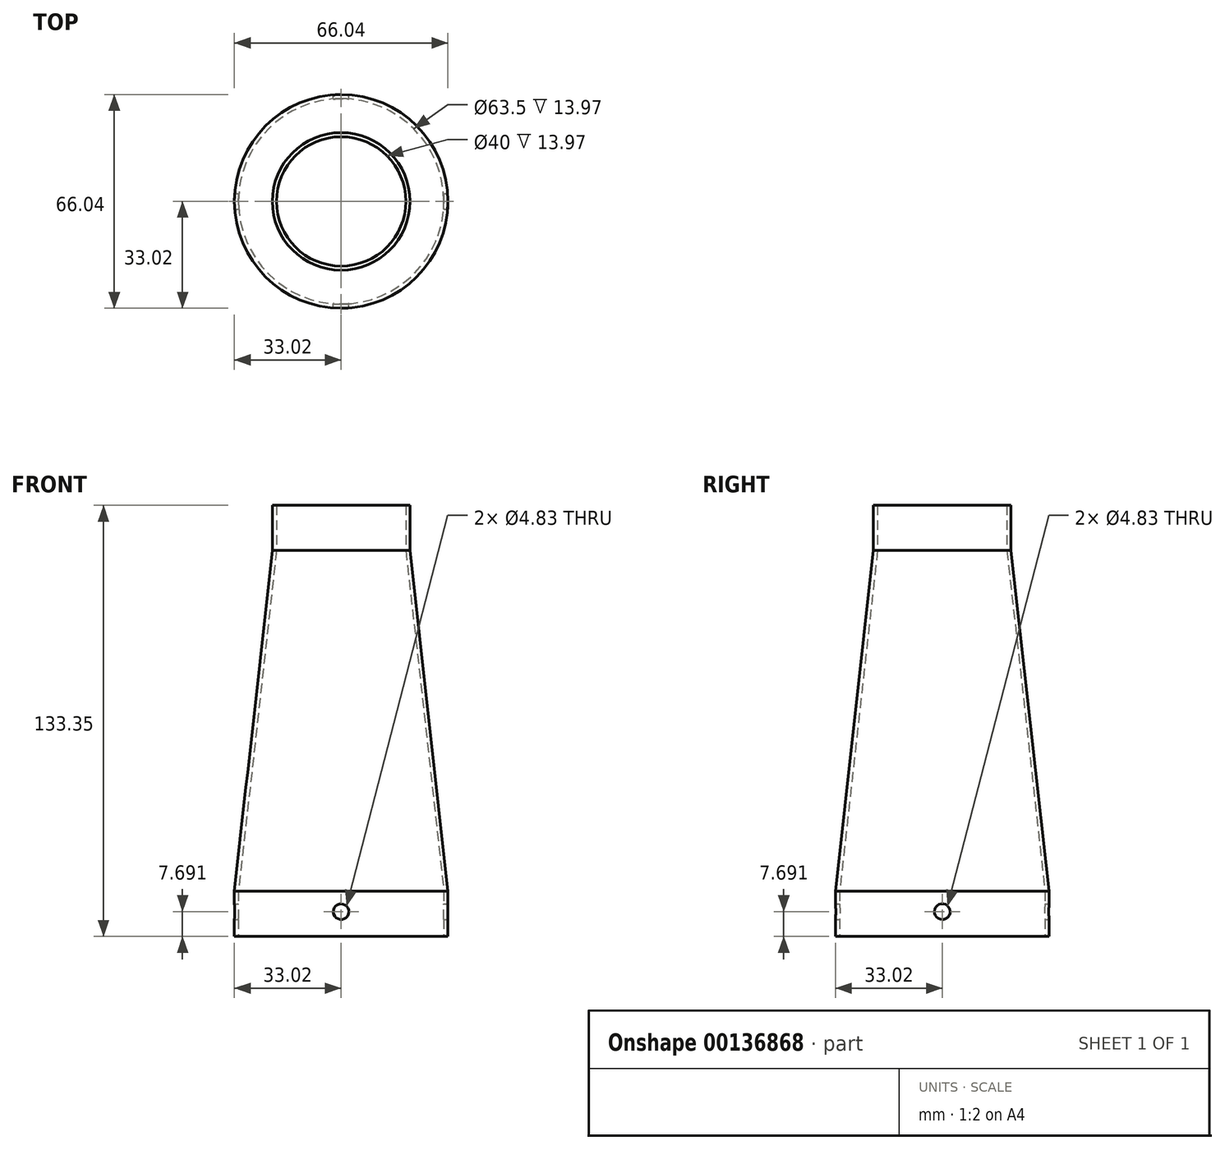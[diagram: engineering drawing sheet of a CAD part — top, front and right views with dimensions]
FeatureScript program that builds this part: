
annotation { "Feature Type Name" : "Feature", "Feature Type Description" : "" }
export const myFeature = defineFeature(function(context is Context, id is Id, definition is map)
    precondition{}
    {
        {
            var Q0;
            Q0=qCreatedBy(makeId("Front.planeOp"),FACE);
            var sketch = newSketch(context, id + "F0", { "sketchPlane" : qUnion([Q0])});
            skLineSegment(sketch, "E0", {"start": v(31.75, 0) * mm, "end": v(31.75, 13.97) * mm});
            skLineSegment(sketch, "E1", {"start": v(31.75, 13.97) * mm, "end": v(20, 119.38) * mm});
            skLineSegment(sketch, "E2", {"start": v(20, 119.38) * mm, "end": v(20, 133.35) * mm});
            skLineSegment(sketch, "E3.0", {"start": v(21.27, 119.45) * mm, "end": v(21.27, 133.35) * mm});
            skLineSegment(sketch, "E3.1", {"start": v(33.02, 14.04) * mm, "end": v(21.27, 119.45) * mm});
            skLineSegment(sketch, "E3.2", {"start": v(33.02, 0) * mm, "end": v(33.02, 14.04) * mm});
            skLineSegment(sketch, "E4", {"start": v(20, 133.35) * mm, "end": v(21.27, 133.35) * mm});
            skLineSegment(sketch, "E5", {"start": v(31.75, 0) * mm, "end": v(33.02, 0) * mm});
            skLineSegment(sketch, "E6", {"start": v(0, 0) * mm, "end": v(0, 49.91) * mm, "construction": true});
            skSolve(sketch);
        }
        {
            var Q0;
            Q0=makeQuery(id+"F0.imprint","IMPRINT",FACE,{"disambiguationData":[TD([[makeQuery(id+"F0.imprint","IMPRINT",EDGE,{"derivedFrom":sQuery(id+"F0.wireOp",EDGE,"E0")}),-1.0]])]});
            var Q1;
            Q1=sQuery(id+"F0.wireOp",EDGE,"E3.1");
            var Q2;
            Q2=sQuery(id+"F0.wireOp",EDGE,"E3.2");
            var Q3;
            Q3=sQuery(id+"F0.wireOp",EDGE,"E3.0");
            var Q4;
            Q4=sQuery(id+"F0.wireOp",EDGE,"E2");
            var Q5;
            Q5=sQuery(id+"F0.wireOp",EDGE,"E1");
            var Q6;
            Q6=sQuery(id+"F0.wireOp",EDGE,"E0");
            var Q7;
            Q7=sQuery(id+"F0.wireOp",EDGE,"E5");
            var Q8;
            Q8=sQuery(id+"F0.wireOp",EDGE,"E4");
            var Q9;
            Q9=sQuery(id+"F0.wireOp",EDGE,"E6");
            revolve(context, id + "F1", {"entities" : qUnion([Q0]), "surfaceEntities" : qUnion([Q1, Q2, Q3, Q4, Q5, Q6, Q7, Q8]), "axis" : qUnion([Q9]), "revolveType" : RevolveType.FULL});
        }
        {
            var Q0;
            Q0=qCreatedBy(makeId("Front.planeOp"),FACE);
            var sketch = newSketch(context, id + "F2", { "sketchPlane" : qUnion([Q0])});
            skCircle(sketch, "E7", {"center": v(0, 7.7) * mm, "radius": 2.41 * mm});
            skSolve(sketch);
        }
        {
            var Q0;
            Q0=qCreatedBy(makeId("Right.planeOp"),FACE);
            var sketch = newSketch(context, id + "F3", { "sketchPlane" : qUnion([Q0])});
            skCircle(sketch, "E8", {"center": v(0, 7.7) * mm, "radius": 2.41 * mm});
            skSolve(sketch);
        }
        {
            var Q0;
            Q0 = qSketchRegion(id + "F2", true);
            extrude(context, id + "F4", {"entities" : qUnion([Q0]), "operationType" : NewBodyOperationType.REMOVE, "endBound" : BoundingType.SYMMETRIC, "depth" : 101.6 * mm});
        }
        {
            var Q0;
            Q0 = qSketchRegion(id + "F3", true);
            extrude(context, id + "F5", {"entities" : qUnion([Q0]), "operationType" : NewBodyOperationType.REMOVE, "endBound" : BoundingType.SYMMETRIC, "oppositeDirection" : true, "depth" : 101.6 * mm});
        }
    });
